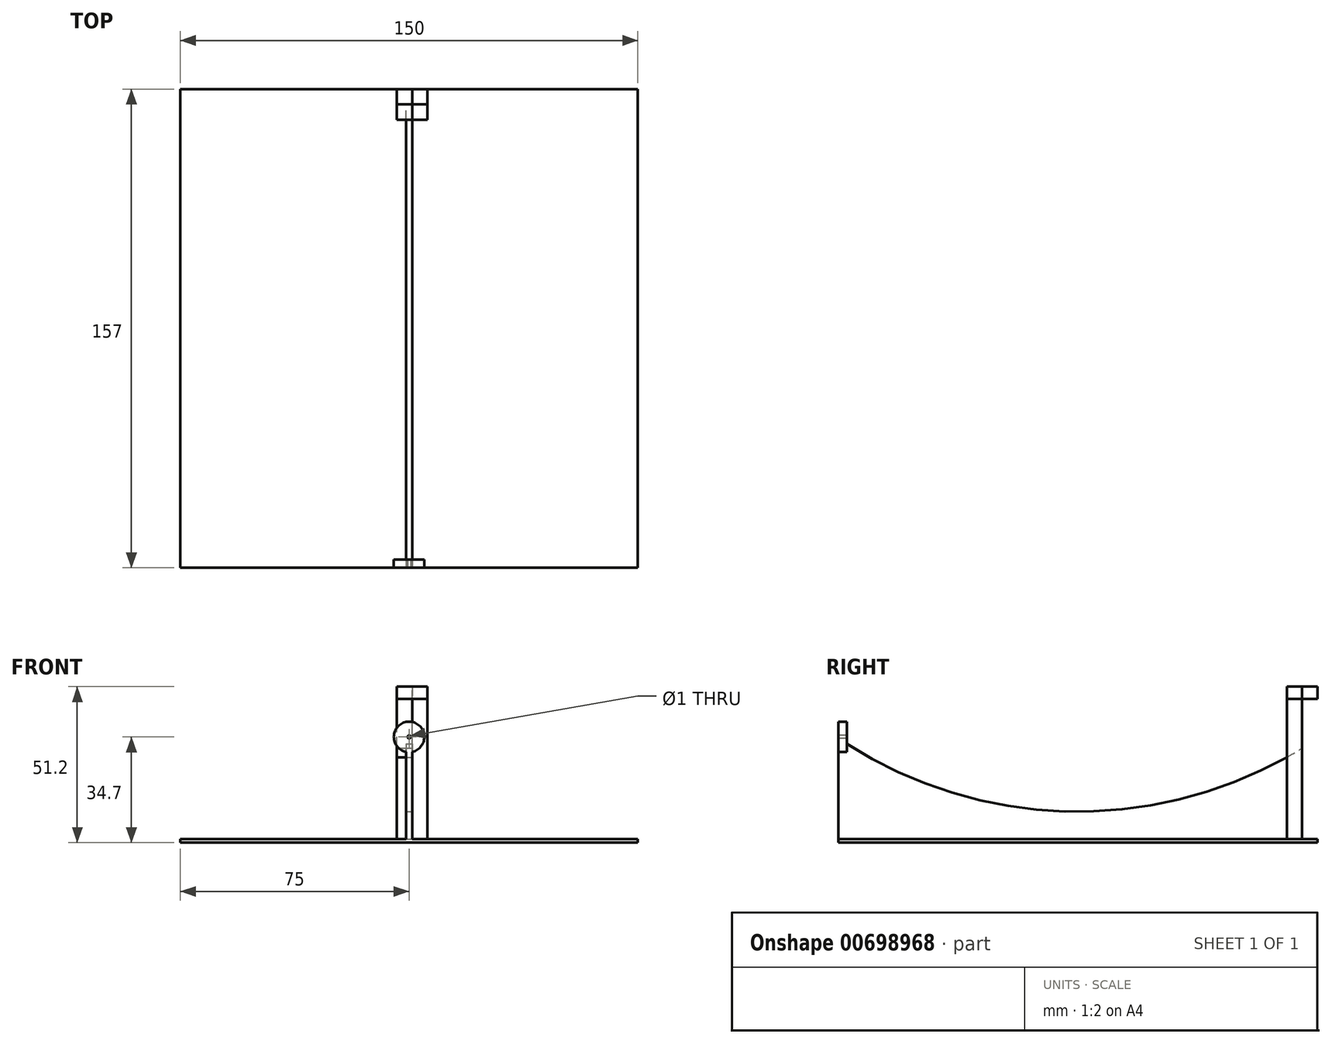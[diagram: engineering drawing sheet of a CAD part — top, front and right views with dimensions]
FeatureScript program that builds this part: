
annotation { "Feature Type Name" : "Feature", "Feature Type Description" : "" }
export const myFeature = defineFeature(function(context is Context, id is Id, definition is map)
    precondition{}
    {
        {
            var Q0;
            Q0=qCreatedBy(makeId("Top.planeOp"),FACE);
            var sketch = newSketch(context, id + "F0", { "sketchPlane" : qUnion([Q0])});
            skLineSegment(sketch, "E0.bottom", {"start": v(-75, 78.5) * mm, "end": v(75, 78.5) * mm});
            skLineSegment(sketch, "E0.top", {"start": v(-75, -78.5) * mm, "end": v(75, -78.5) * mm});
            skLineSegment(sketch, "E0.left", {"start": v(-75, 78.5) * mm, "end": v(-75, -78.5) * mm});
            skLineSegment(sketch, "E0.right", {"start": v(75, 78.5) * mm, "end": v(75, -78.5) * mm});
            skPoint(sketch, "E0.middle", {"position": v(0, 0) * mm});
            skSolve(sketch);
        }
        {
            var Q0;
            Q0 = qSketchRegion(id + "F0", true);
            extrude(context, id + "F1", {"entities" : qUnion([Q0]), "oppositeDirection" : true, "depth" : 1.2 * mm, "offsetDistance" : 25.4 * mm});
        }
        {
            var Q0;
            Q0=makeQuery(id+"F1.opExtrude","CAP_FACE",FACE,{"disambiguationData":[OSD([sQuery(id+"F0.wireOp",EDGE,"E0.bottom"),sQuery(id+"F0.wireOp",EDGE,"E0.top"),sQuery(id+"F0.wireOp",EDGE,"E0.left"),sQuery(id+"F0.wireOp",EDGE,"E0.right")])],"isStart":true});
            var sketch = newSketch(context, id + "F2", { "sketchPlane" : qUnion([Q0])});
            skLineSegment(sketch, "E1.bottom", {"start": v(-1, 78.5) * mm, "end": v(1, 78.5) * mm});
            skLineSegment(sketch, "E1.top", {"start": v(-1, -78.5) * mm, "end": v(1, -78.5) * mm});
            skLineSegment(sketch, "E1.left", {"start": v(-1, 78.5) * mm, "end": v(-1, -78.5) * mm});
            skLineSegment(sketch, "E1.right", {"start": v(1, 78.5) * mm, "end": v(1, -78.5) * mm});
            skPoint(sketch, "E1.middle", {"position": v(0, 0) * mm});
            skSolve(sketch);
        }
        {
            var Q0;
            Q0=makeQuery(id+"F2.imprint","IMPRINT",FACE,{"disambiguationData":[TD([[makeQuery(id+"F2.imprint","IMPRINT",EDGE,{"derivedFrom":sQuery(id+"F2.wireOp",EDGE,"E1.bottom")}),-1.0]])]});
            extrude(context, id + "F3", {"entities" : qUnion([Q0]), "operationType" : NewBodyOperationType.ADD, "depth" : 33 * mm, "offsetDistance" : 25 * mm});
        }
        {
            var Q0;
            Q0=makeQuery(id+"F3.opExtrude","SWEPT_FACE",FACE,{"disambiguationData":[OSD([sQuery(id+"F2.wireOp",EDGE,"E1.right")])]});
            var sketch = newSketch(context, id + "F4", { "sketchPlane" : qUnion([Q0])});
            skArc(sketch, "E2", {"start": v(-78.5, 33) * mm, "mid": v(0, 9) * mm, "end": v(78.5, 33) * mm});
            skSolve(sketch);
        }
        {
            var Q0;
            Q0=makeQuery(id+"F4.imprint","IMPRINT",FACE,{"disambiguationData":[TD([[makeQuery(id+"F4.imprint","IMPRINT",EDGE,{"derivedFrom":sQuery(id+"F4.wireOp",EDGE,"E2")}),1.0]])]});
            extrude(context, id + "F5", {"entities" : qUnion([Q0]), "operationType" : NewBodyOperationType.REMOVE, "oppositeDirection" : true, "depth" : 2 * mm, "offsetDistance" : 25 * mm});
        }
        {
            var Q0;
            Q0=makeQuery(id+"F3.opExtrude","SWEPT_FACE",FACE,{"disambiguationData":[OSD([sQuery(id+"F2.wireOp",EDGE,"E1.right")])]});
            var sketch = newSketch(context, id + "F6", { "sketchPlane" : qUnion([Q0])});
            skLineSegment(sketch, "E3.bottom", {"start": v(73.5, 0) * mm, "end": v(68.5, 0) * mm});
            skLineSegment(sketch, "E3.top", {"start": v(73.5, 50) * mm, "end": v(68.5, 50) * mm});
            skLineSegment(sketch, "E3.left", {"start": v(73.5, 0) * mm, "end": v(73.5, 50) * mm});
            skLineSegment(sketch, "E3.right", {"start": v(68.5, 0) * mm, "end": v(68.5, 50) * mm});
            skLineSegment(sketch, "E4.bottom", {"start": v(68.5, 50) * mm, "end": v(78.5, 50) * mm});
            skLineSegment(sketch, "E4.top", {"start": v(68.5, 46) * mm, "end": v(78.5, 46) * mm});
            skLineSegment(sketch, "E4.left", {"start": v(68.5, 50) * mm, "end": v(68.5, 46) * mm});
            skLineSegment(sketch, "E4.right", {"start": v(78.5, 50) * mm, "end": v(78.5, 46) * mm});
            skSolve(sketch);
        }
        {
            var Q0;
            {var subQ0=sQuery(id+"F6.wireOp",EDGE,"E3.bottom");Q0=makeQuery(id+"F6.imprint","IMPRINT",FACE,{"disambiguationData":[TD([[makeQuery(id+"F6.imprint","IMPRINT",EDGE,{"derivedFrom":subQ0}),-1.0]])]});}
            var Q1;
            {var subQ0=sQuery(id+"F6.wireOp",EDGE,"E4.top");var subQ1=sQuery(id+"F6.wireOp",EDGE,"E3.left");var subQ2=makeQuery(id+"F6.imprint","INTERSECT",VERTEX,{"derivedFrom":[subQ1,subQ0]});Q1=makeQuery(id+"F6.imprint","IMPRINT",FACE,{"disambiguationData":[TD([[makeQuery(id+"F6.imprint","IMPRINT",EDGE,{"disambiguationData":[TD([[subQ2,1.0]])],"derivedFrom":subQ1}),1.0]])]});}
            var Q2;
            {var subQ5=sQuery(id+"F6.wireOp",EDGE,"E4.left");Q2=makeQuery(id+"F6.imprint","IMPRINT",FACE,{"disambiguationData":[TD([[makeQuery(id+"F6.imprint","IMPRINT",EDGE,{"derivedFrom":subQ5}),1.0]])]});}
            var Q3;
            {var subQ5=sQuery(id+"F6.wireOp",EDGE,"E4.right");Q3=makeQuery(id+"F6.imprint","IMPRINT",FACE,{"disambiguationData":[TD([[makeQuery(id+"F6.imprint","IMPRINT",EDGE,{"derivedFrom":subQ5}),-1.0]])]});}
            extrude(context, id + "F7", {"entities" : qUnion([Q0, Q1, Q2, Q3]), "operationType" : NewBodyOperationType.ADD, "depth" : 5 * mm, "offsetDistance" : 25 * mm});
        }
        {
            var Q0;
            Q0=makeQuery(id+"F7.opExtrude","CAP_FACE",FACE,{"disambiguationData":[OSD([sQuery(id+"F6.wireOp",EDGE,"E3.bottom"),sQuery(id+"F6.wireOp",EDGE,"E3.left"),sQuery(id+"F6.wireOp",EDGE,"E3.right"),sQuery(id+"F6.wireOp",EDGE,"E4.bottom"),sQuery(id+"F6.wireOp",EDGE,"E4.top"),sQuery(id+"F6.wireOp",EDGE,"E4.left"),sQuery(id+"F6.wireOp",EDGE,"E4.right")])],"isStart":true});
            var Q1;
            Q1 = qSketchRegion(id + "F6", true);
            extrude(context, id + "F8", {"entities" : qUnion([Q0, Q1]), "depth" : 5 * mm, "offsetDistance" : 25 * mm});
        }
        {
            var Q0;
            {var subQ1=sQuery(id+"F2.wireOp",EDGE,"E1.right");var subQ6=makeQuery(id+"F3.opExtrude","SWEPT_EDGE",EDGE,{"disambiguationData":[OSD([sQuery(id+"F0.wireOp",EDGE,"E0.bottom"),sQuery(id+"F2.wireOp",EDGE,"E1.bottom"),subQ1])]});Q0=makeQuery(id+"F6.imprint","IMPRINT",FACE,{"disambiguationData":[TD([[makeQuery(id+"F6.imprint","IMPRINT",EDGE,{"derivedFrom":subQ6}),-1.0]])]});}
            extrude(context, id + "F9", {"entities" : qUnion([Q0]), "operationType" : NewBodyOperationType.REMOVE, "oppositeDirection" : true, "depth" : 1.8 * mm, "offsetDistance" : 25 * mm});
        }
        {
            var Q0;
            {var subQ0=sQuery(id+"F6.wireOp",EDGE,"E3.left");var subQ1=makeQuery(id+"F6.imprint","INTERSECT",VERTEX,{"derivedFrom":[makeQuery(id+"F5.boolean.opBoolean","COPY",EDGE,{"derivedFrom":makeQuery(id+"F5.opExtrude","CAP_EDGE",EDGE,{"disambiguationData":[OSD([sQuery(id+"F4.wireOp",EDGE,"E2")])],"isStart":true})}),subQ0]});Q0=makeQuery(id+"F8.opExtrude","SWEPT_FACE",FACE,{"disambiguationData":[OSD([subQ0]),TDD([makeQuery(id+"F6.imprint","IMPRINT",EDGE,{"disambiguationData":[TD([[subQ1,1.0]])],"derivedFrom":subQ0}),makeQuery(id+"F6.imprint","IMPRINT",EDGE,{"disambiguationData":[TD([[makeQuery(id+"F6.imprint","INTERSECT",VERTEX,{"derivedFrom":[subQ0,sQuery(id+"F6.wireOp",EDGE,"E4.top")]}),1.0]])],"derivedFrom":subQ0})])]});}
            extrude(context, id + "F10", {"entities" : qUnion([Q0]), "operationType" : NewBodyOperationType.REMOVE, "depth" : 5.1 * mm, "offsetDistance" : 25 * mm});
        }
        {
            var Q0;
            Q0=makeQuery(id+"F3.boolean.opBoolean","MERGE",FACE,{"derivedFrom":[makeQuery(id+"F1.opExtrude","SWEPT_FACE",FACE,{"disambiguationData":[OSD([sQuery(id+"F0.wireOp",EDGE,"E0.top")])]}),makeQuery(id+"F3.opExtrude","SWEPT_FACE",FACE,{"disambiguationData":[OSD([sQuery(id+"F2.wireOp",EDGE,"E1.top")])]})]});
            var sketch = newSketch(context, id + "F11", { "sketchPlane" : qUnion([Q0])});
            skCircle(sketch, "E5", {"center": v(0, 33.5) * mm, "radius": 0.5 * mm});
            skCircle(sketch, "E6", {"center": v(0, 33.5) * mm, "radius": 5 * mm});
            skSolve(sketch);
        }
        {
            var Q0;
            {var subQ8=sQuery(id+"F11.wireOp",EDGE,"E5");Q0=makeQuery(id+"F11.imprint","IMPRINT",FACE,{"disambiguationData":[TD([[makeQuery(id+"F11.imprint","IMPRINT",EDGE,{"derivedFrom":subQ8}),-1.0]])]});}
            var Q1;
            {var subQ1=sQuery(id+"F2.wireOp",EDGE,"E1.top");var subQ2=sQuery(id+"F0.wireOp",EDGE,"E0.top");var subQ4=makeQuery(id+"F3.opExtrude","SWEPT_EDGE",EDGE,{"disambiguationData":[OSD([subQ2,subQ1,sQuery(id+"F2.wireOp",EDGE,"E1.left")])]});var subQ7=sQuery(id+"F11.wireOp",EDGE,"E6");var subQ8=makeQuery(id+"F11.imprint","INTERSECT",VERTEX,{"derivedFrom":[subQ4,subQ7]});Q1=makeQuery(id+"F11.imprint","IMPRINT",FACE,{"disambiguationData":[TD([[makeQuery(id+"F11.imprint","IMPRINT",EDGE,{"disambiguationData":[TD([[subQ8,-1.0]])],"derivedFrom":subQ7}),1.0]])]});}
            extrude(context, id + "F12", {"entities" : qUnion([Q0, Q1]), "operationType" : NewBodyOperationType.ADD, "oppositeDirection" : true, "depth" : 2.7 * mm, "offsetDistance" : 25 * mm});
        }
    });
